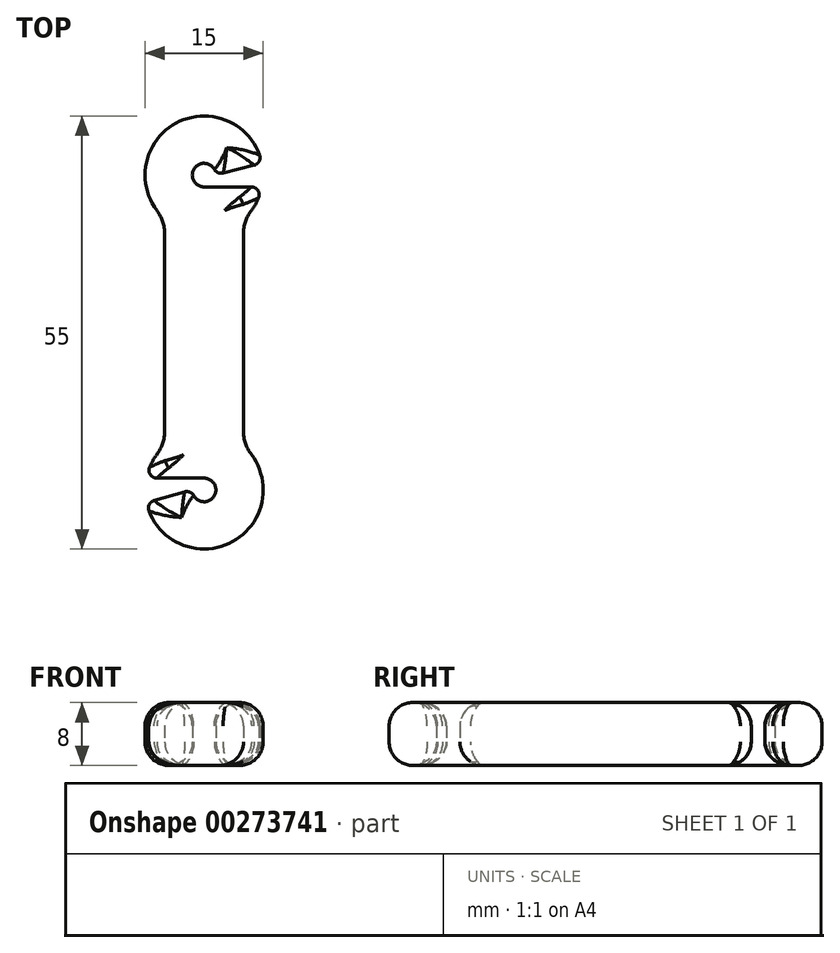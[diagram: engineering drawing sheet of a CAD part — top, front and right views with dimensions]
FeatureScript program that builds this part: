
annotation { "Feature Type Name" : "Feature", "Feature Type Description" : "" }
export const myFeature = defineFeature(function(context is Context, id is Id, definition is map)
    precondition{}
    {
        {
            var Q0;
            Q0=qCreatedBy(makeId("Top.planeOp"),FACE);
            var sketch = newSketch(context, id + "F0", { "sketchPlane" : qUnion([Q0])});
            skArc(sketch, "E0", {"start": v(6, 15.5) * mm, "mid": v(6.51, 16.28) * mm, "end": v(6.92, 17.12) * mm});
            skArc(sketch, "E1.MirrorC", {"start": v(6, -15.5) * mm, "mid": v(3.62, -26.57) * mm, "end": v(-7.01, -22.66) * mm});
            skLineSegment(sketch, "E2", {"start": v(5, 12.5) * mm, "end": v(5, -12.5) * mm});
            skLineSegment(sketch, "E3.MirrorCS", {"start": v(-5, 12.5) * mm, "end": v(-5, -12.5) * mm});
            skPoint(sketch, "E4.visualSharp", {"position": v(5, 14.4) * mm});
            skArc(sketch, "E4.filletArc", {"start": v(6, 15.5) * mm, "mid": v(5.26, 14.08) * mm, "end": v(5, 12.5) * mm});
            skPoint(sketch, "E5.visualSharp", {"position": v(-5, 14.4) * mm});
            skArc(sketch, "E5.filletArc", {"start": v(-5, 12.5) * mm, "mid": v(-5.26, 14.08) * mm, "end": v(-6, 15.5) * mm});
            skPoint(sketch, "E6.visualSharp", {"position": v(-5, -14.4) * mm});
            skArc(sketch, "E6.filletArc", {"start": v(-6, -15.5) * mm, "mid": v(-5.26, -14.08) * mm, "end": v(-5, -12.5) * mm});
            skPoint(sketch, "E7.visualSharp", {"position": v(5, -14.4) * mm});
            skArc(sketch, "E7.filletArc", {"start": v(5, -12.5) * mm, "mid": v(5.26, -14.08) * mm, "end": v(6, -15.5) * mm});
            skArc(sketch, "E8", {"start": v(1.3, 20.74) * mm, "mid": v(-1.3, 20.76) * mm, "end": v(0, 18.5) * mm});
            skArc(sketch, "E9.MirrorC", {"start": v(0, -18.5) * mm, "mid": v(1.3, -20.76) * mm, "end": v(-1.31, -20.72) * mm});
            skLineSegment(sketch, "E10", {"start": v(0, -18.5) * mm, "end": v(-6, -18.5) * mm});
            skLineSegment(sketch, "E11", {"start": v(-2.46, -20.25) * mm, "end": v(-6.35, -21.34) * mm});
            skLineSegment(sketch, "E12", {"start": v(0, 18.5) * mm, "end": v(6, 18.5) * mm});
            skLineSegment(sketch, "E13", {"start": v(2.42, 20.26) * mm, "end": v(6.35, 21.25) * mm});
            skArc(sketch, "E14.trimOffspring", {"start": v(7.05, 22.56) * mm, "mid": v(-3.57, 26.6) * mm, "end": v(-6, 15.5) * mm});
            skArc(sketch, "E15.trimOffspring", {"start": v(-6.92, -17.12) * mm, "mid": v(-6.51, -16.28) * mm, "end": v(-6, -15.5) * mm});
            skPoint(sketch, "E16.visualSharp", {"position": v(1.5, 20.03) * mm});
            skArc(sketch, "E16.filletArc", {"start": v(1.3, 20.74) * mm, "mid": v(1.78, 20.31) * mm, "end": v(2.42, 20.26) * mm});
            skPoint(sketch, "E17.visualSharp", {"position": v(7.35, 21.5) * mm});
            skArc(sketch, "E17.filletArc", {"start": v(6.35, 21.25) * mm, "mid": v(7, 21.75) * mm, "end": v(7.05, 22.56) * mm});
            skPoint(sketch, "E18.visualSharp", {"position": v(7.35, 18.5) * mm});
            skArc(sketch, "E18.filletArc", {"start": v(6.92, 17.12) * mm, "mid": v(6.83, 18.05) * mm, "end": v(6, 18.5) * mm});
            skPoint(sketch, "E19.visualSharp", {"position": v(-7.35, -18.5) * mm});
            skArc(sketch, "E19.filletArc", {"start": v(-6.92, -17.12) * mm, "mid": v(-6.83, -18.05) * mm, "end": v(-6, -18.5) * mm});
            skPoint(sketch, "E20.visualSharp", {"position": v(-7.32, -21.62) * mm});
            skArc(sketch, "E20.filletArc", {"start": v(-6.35, -21.34) * mm, "mid": v(-6.97, -21.86) * mm, "end": v(-7.01, -22.66) * mm});
            skPoint(sketch, "E21.visualSharp", {"position": v(-1.5, -19.97) * mm});
            skArc(sketch, "E21.filletArc", {"start": v(-1.31, -20.72) * mm, "mid": v(-1.8, -20.29) * mm, "end": v(-2.46, -20.25) * mm});
            skSolve(sketch);
        }
        {
            var Q0;
            Q0=makeQuery(id+"F0.imprint","IMPRINT",FACE,{"disambiguationData":[TD([[makeQuery(id+"F0.imprint","IMPRINT",EDGE,{"derivedFrom":sQuery(id+"F0.wireOp",EDGE,"E0")}),1.0]])]});
            extrude(context, id + "F1", {"entities" : qUnion([Q0]), "depth" : 8 * mm});
        }
        {
            var Q0;
            Q0=makeQuery(id+"F1.opExtrude","CAP_FACE",FACE,{"disambiguationData":[OSD([sQuery(id+"F0.wireOp",EDGE,"E0"),sQuery(id+"F0.wireOp",EDGE,"E1.MirrorC"),sQuery(id+"F0.wireOp",EDGE,"E2"),sQuery(id+"F0.wireOp",EDGE,"E3.MirrorCS"),sQuery(id+"F0.wireOp",EDGE,"E4.filletArc"),sQuery(id+"F0.wireOp",EDGE,"E5.filletArc"),sQuery(id+"F0.wireOp",EDGE,"E6.filletArc"),sQuery(id+"F0.wireOp",EDGE,"E7.filletArc"),sQuery(id+"F0.wireOp",EDGE,"E8"),sQuery(id+"F0.wireOp",EDGE,"E9.MirrorC"),sQuery(id+"F0.wireOp",EDGE,"E10"),sQuery(id+"F0.wireOp",EDGE,"E11"),sQuery(id+"F0.wireOp",EDGE,"E12"),sQuery(id+"F0.wireOp",EDGE,"E13"),sQuery(id+"F0.wireOp",EDGE,"E14.trimOffspring"),sQuery(id+"F0.wireOp",EDGE,"E15.trimOffspring"),sQuery(id+"F0.wireOp",EDGE,"E16.filletArc"),sQuery(id+"F0.wireOp",EDGE,"E17.filletArc"),sQuery(id+"F0.wireOp",EDGE,"E18.filletArc"),sQuery(id+"F0.wireOp",EDGE,"E19.filletArc"),sQuery(id+"F0.wireOp",EDGE,"E20.filletArc"),sQuery(id+"F0.wireOp",EDGE,"E21.filletArc")])],"isStart":false});
            var Q1;
            Q1=makeQuery(id+"F1.opExtrude","CAP_FACE",FACE,{"disambiguationData":[OSD([sQuery(id+"F0.wireOp",EDGE,"E0"),sQuery(id+"F0.wireOp",EDGE,"E1.MirrorC"),sQuery(id+"F0.wireOp",EDGE,"E2"),sQuery(id+"F0.wireOp",EDGE,"E3.MirrorCS"),sQuery(id+"F0.wireOp",EDGE,"E4.filletArc"),sQuery(id+"F0.wireOp",EDGE,"E5.filletArc"),sQuery(id+"F0.wireOp",EDGE,"E6.filletArc"),sQuery(id+"F0.wireOp",EDGE,"E7.filletArc"),sQuery(id+"F0.wireOp",EDGE,"E8"),sQuery(id+"F0.wireOp",EDGE,"E9.MirrorC"),sQuery(id+"F0.wireOp",EDGE,"E10"),sQuery(id+"F0.wireOp",EDGE,"E11"),sQuery(id+"F0.wireOp",EDGE,"E12"),sQuery(id+"F0.wireOp",EDGE,"E13"),sQuery(id+"F0.wireOp",EDGE,"E14.trimOffspring"),sQuery(id+"F0.wireOp",EDGE,"E15.trimOffspring"),sQuery(id+"F0.wireOp",EDGE,"E16.filletArc"),sQuery(id+"F0.wireOp",EDGE,"E17.filletArc"),sQuery(id+"F0.wireOp",EDGE,"E18.filletArc"),sQuery(id+"F0.wireOp",EDGE,"E19.filletArc"),sQuery(id+"F0.wireOp",EDGE,"E20.filletArc"),sQuery(id+"F0.wireOp",EDGE,"E21.filletArc")])],"isStart":true});
            fillet(context, id + "F2", {"entities" : qUnion([Q0, Q1]), "radius" : 3 * mm, "tangentPropagation" : true, "allowEdgeOverflow" : false});
        }
    });
